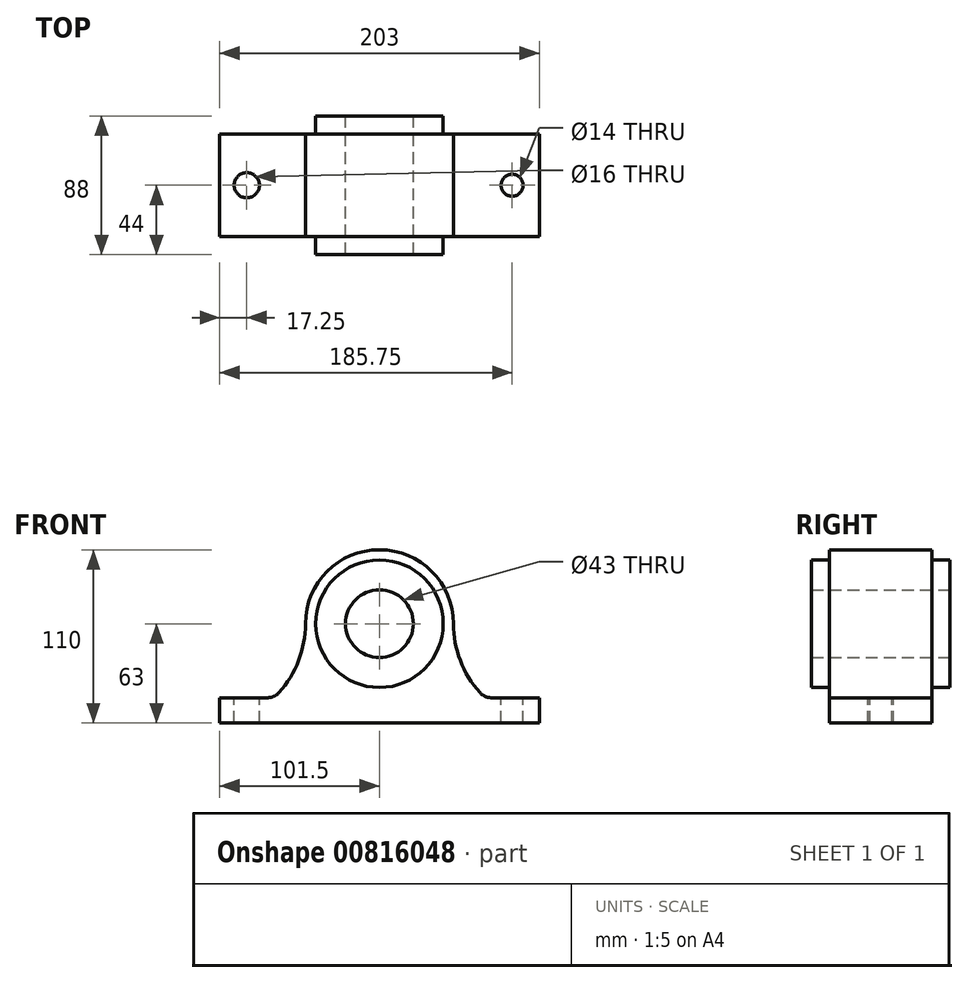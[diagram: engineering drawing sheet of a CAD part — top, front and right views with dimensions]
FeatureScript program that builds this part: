
annotation { "Feature Type Name" : "Feature", "Feature Type Description" : "" }
export const myFeature = defineFeature(function(context is Context, id is Id, definition is map)
    precondition{}
    {
        {
            var Q0;
            Q0=qCreatedBy(makeId("Front.planeOp"),FACE);
            var sketch = newSketch(context, id + "F0", { "sketchPlane" : qUnion([Q0])});
            skLineSegment(sketch, "E0", {"start": v(0, 0) * mm, "end": v(0, 110) * mm});
            skLineSegment(sketch, "E1", {"start": v(0, 0) * mm, "end": v(101.5, 0) * mm, "construction": true});
            skLineSegment(sketch, "E2", {"start": v(0, 0) * mm, "end": v(0, 16) * mm, "construction": true});
            skLineSegment(sketch, "E3.bottom", {"start": v(0, 0) * mm, "end": v(101.5, 0) * mm});
            skLineSegment(sketch, "E3.top", {"start": v(47, 16) * mm, "end": v(101.5, 16) * mm});
            skLineSegment(sketch, "E3.left", {"start": v(0, 0) * mm, "end": v(0, 16) * mm});
            skLineSegment(sketch, "E3.right", {"start": v(101.5, 0) * mm, "end": v(101.5, 16) * mm});
            skLineSegment(sketch, "E4.bottom", {"start": v(0, 0) * mm, "end": v(-101.5, 0) * mm});
            skLineSegment(sketch, "E4.top", {"start": v(-67, 16) * mm, "end": v(-101.5, 16) * mm});
            skLineSegment(sketch, "E4.right", {"start": v(-101.5, 0) * mm, "end": v(-101.5, 16) * mm});
            skLineSegment(sketch, "E5", {"start": v(0, 110) * mm, "end": v(0, 63) * mm});
            skCircle(sketch, "E6", {"center": v(0, 63) * mm, "radius": 21.5 * mm});
            skArc(sketch, "E7", {"start": v(47, 63) * mm, "mid": v(0, 110) * mm, "end": v(-47, 63) * mm});
            skLineSegment(sketch, "E8", {"start": v(0, 63) * mm, "end": v(-47, 63) * mm, "construction": true});
            skLineSegment(sketch, "E9", {"start": v(0, 63) * mm, "end": v(47, 63) * mm, "construction": true});
            skLineSegment(sketch, "E10", {"start": v(47, 63) * mm, "end": v(47, 16) * mm, "construction": true});
            skLineSegment(sketch, "E11", {"start": v(-47, 63) * mm, "end": v(-47, 16) * mm, "construction": true});
            skArc(sketch, "E12", {"start": v(-67, 16) * mm, "mid": v(-52.2, 37.46) * mm, "end": v(-47, 63) * mm});
            skArc(sketch, "E13", {"start": v(47, 63) * mm, "mid": v(52.2, 37.46) * mm, "end": v(67, 16) * mm});
            skSolve(sketch);
        }
        {
            var Q0;
            Q0=makeQuery(id+"F0.imprint","IMPRINT",FACE,{"disambiguationData":[TD([[makeQuery(id+"F0.imprint","IMPRINT",EDGE,{"derivedFrom":sQuery(id+"F0.wireOp",EDGE,"E3.bottom")}),1.0]])]});
            var Q1;
            Q1=makeQuery(id+"F0.imprint","IMPRINT",FACE,{"disambiguationData":[TD([[makeQuery(id+"F0.imprint","IMPRINT",EDGE,{"derivedFrom":sQuery(id+"F0.wireOp",EDGE,"E4.bottom")}),-1.0]])]});
            extrude(context, id + "F1", {"entities" : qUnion([Q0, Q1]), "depth" : 65 * mm, "offsetDistance" : 25 * mm});
        }
        {
            var Q0;
            Q0=makeQuery(id+"F1.opExtrude","CAP_FACE",FACE,{"disambiguationData":[OSD([sQuery(id+"F0.wireOp",EDGE,"E3.bottom"),sQuery(id+"F0.wireOp",EDGE,"E3.top"),sQuery(id+"F0.wireOp",EDGE,"E3.right"),sQuery(id+"F0.wireOp",EDGE,"E4.bottom"),sQuery(id+"F0.wireOp",EDGE,"E4.top"),sQuery(id+"F0.wireOp",EDGE,"E4.right"),sQuery(id+"F0.wireOp",EDGE,"E6"),sQuery(id+"F0.wireOp",EDGE,"E7"),sQuery(id+"F0.wireOp",EDGE,"E12"),sQuery(id+"F0.wireOp",EDGE,"E13")])],"isStart":false});
            var sketch = newSketch(context, id + "F2", { "sketchPlane" : qUnion([Q0])});
            skLineSegment(sketch, "E14", {"start": v(0, 0) * mm, "end": v(0, 63) * mm, "construction": true});
            skCircle(sketch, "E15", {"center": v(0, 63) * mm, "radius": 40.5 * mm});
            skCircle(sketch, "E16", {"center": v(0, 63) * mm, "radius": 21.5 * mm});
            skSolve(sketch);
        }
        {
            var Q0;
            Q0=makeQuery(id+"F2.imprint","IMPRINT",FACE,{"disambiguationData":[TD([[makeQuery(id+"F2.imprint","IMPRINT",EDGE,{"derivedFrom":sQuery(id+"F2.wireOp",EDGE,"E15")}),1.0]])]});
            extrude(context, id + "F3", {"entities" : qUnion([Q0]), "operationType" : NewBodyOperationType.ADD, "depth" : 11.5 * mm, "offsetDistance" : 25 * mm});
        }
        {
            var Q0;
            Q0=makeQuery(id+"F1.opExtrude","CAP_FACE",FACE,{"disambiguationData":[OSD([sQuery(id+"F0.wireOp",EDGE,"E3.bottom"),sQuery(id+"F0.wireOp",EDGE,"E3.top"),sQuery(id+"F0.wireOp",EDGE,"E3.right"),sQuery(id+"F0.wireOp",EDGE,"E4.bottom"),sQuery(id+"F0.wireOp",EDGE,"E4.top"),sQuery(id+"F0.wireOp",EDGE,"E4.right"),sQuery(id+"F0.wireOp",EDGE,"E6"),sQuery(id+"F0.wireOp",EDGE,"E7"),sQuery(id+"F0.wireOp",EDGE,"E12"),sQuery(id+"F0.wireOp",EDGE,"E13")])],"isStart":true});
            var sketch = newSketch(context, id + "F4", { "sketchPlane" : qUnion([Q0])});
            skLineSegment(sketch, "E17", {"start": v(0, 0) * mm, "end": v(0, 63) * mm, "construction": true});
            skCircle(sketch, "E18", {"center": v(0, 63) * mm, "radius": 40.5 * mm});
            skCircle(sketch, "E19", {"center": v(0, 63) * mm, "radius": 21.5 * mm});
            skSolve(sketch);
        }
        {
            var Q0;
            Q0=makeQuery(id+"F4.imprint","IMPRINT",FACE,{"disambiguationData":[TD([[makeQuery(id+"F4.imprint","IMPRINT",EDGE,{"derivedFrom":sQuery(id+"F4.wireOp",EDGE,"E18")}),1.0]])]});
            extrude(context, id + "F5", {"entities" : qUnion([Q0]), "operationType" : NewBodyOperationType.ADD, "depth" : 11.5 * mm, "offsetDistance" : 25 * mm});
        }
        {
            var Q0;
            Q0=makeQuery(id+"F1.opExtrude","SWEPT_FACE",FACE,{"disambiguationData":[OSD([sQuery(id+"F0.wireOp",EDGE,"E3.top")])]});
            var sketch = newSketch(context, id + "F6", { "sketchPlane" : qUnion([Q0])});
            skLineSegment(sketch, "E20", {"start": v(84.25, 0) * mm, "end": v(84.25, -65) * mm, "construction": true});
            skLineSegment(sketch, "E21", {"start": v(101.5, -32.5) * mm, "end": v(84.25, -32.5) * mm, "construction": true});
            skCircle(sketch, "E22", {"center": v(84.25, -32.5) * mm, "radius": 7 * mm});
            skSolve(sketch);
        }
        {
            var Q0;
            Q0=sQuery(id+"F6.wireOp",VERTEX,"E21.end");
            var Q1;
            Q1=makeQuery(id+"F1.opExtrude","SWEPT_BODY",BODY,{"disambiguationData":[OSD([sQuery(id+"F0.wireOp",EDGE,"E3.bottom"),sQuery(id+"F0.wireOp",EDGE,"E3.top"),sQuery(id+"F0.wireOp",EDGE,"E3.right"),sQuery(id+"F0.wireOp",EDGE,"E4.bottom"),sQuery(id+"F0.wireOp",EDGE,"E4.top"),sQuery(id+"F0.wireOp",EDGE,"E4.right"),sQuery(id+"F0.wireOp",EDGE,"E6"),sQuery(id+"F0.wireOp",EDGE,"E7"),sQuery(id+"F0.wireOp",EDGE,"E12"),sQuery(id+"F0.wireOp",EDGE,"E13")])]});
            hole(context, id + "F7", {"style" : HoleStyle.SIMPLE, "endStyle" : HoleEndStyle.THROUGH, "holeDiameter" : 14 * mm, "majorDiameter" : 5 * mm, "isTappedThrough" : true, "tappedDepth" : 12 * mm, "tapClearance" : 3, "locations" : qUnion([Q0]), "scope" : qUnion([Q1])});
        }
        {
            var Q0;
            Q0=makeQuery(id+"F1.opExtrude","SWEPT_FACE",FACE,{"disambiguationData":[OSD([sQuery(id+"F0.wireOp",EDGE,"E4.top")])]});
            var sketch = newSketch(context, id + "F8", { "sketchPlane" : qUnion([Q0])});
            skLineSegment(sketch, "E23", {"start": v(-101.5, -32.5) * mm, "end": v(-84.25, -32.5) * mm, "construction": true});
            skPoint(sketch, "E23.endSnap0", {"position": v(-84.25, 0) * mm});
            skLineSegment(sketch, "E24", {"start": v(-84.25, -32.5) * mm, "end": v(-84.25, 0) * mm, "construction": true});
            skCircle(sketch, "E25", {"center": v(-84.25, -32.5) * mm, "radius": 7 * mm});
            skSolve(sketch);
        }
        {
            var Q0;
            Q0=makeQuery(id+"F1.opExtrude","SWEPT_EDGE",EDGE,{"disambiguationData":[OSD([sQuery(id+"F0.wireOp",EDGE,"E4.top"),sQuery(id+"F0.wireOp",EDGE,"E12")])]});
            var Q1;
            Q1=makeQuery(id+"F1.opExtrude","SWEPT_EDGE",EDGE,{"disambiguationData":[OSD([sQuery(id+"F0.wireOp",EDGE,"E3.top"),sQuery(id+"F0.wireOp",EDGE,"E13")])]});
            fillet(context, id + "F9", {"entities" : qUnion([Q0, Q1]), "radius" : 10 * mm, "tangentPropagation" : true, "allowEdgeOverflow" : false});
        }
        {
            var Q0;
            Q0=sQuery(id+"F8.wireOp",VERTEX,"E23.end");
            var Q1;
            Q1=makeQuery(id+"F1.opExtrude","SWEPT_BODY",BODY,{"disambiguationData":[OSD([sQuery(id+"F0.wireOp",EDGE,"E3.bottom"),sQuery(id+"F0.wireOp",EDGE,"E3.top"),sQuery(id+"F0.wireOp",EDGE,"E3.right"),sQuery(id+"F0.wireOp",EDGE,"E4.bottom"),sQuery(id+"F0.wireOp",EDGE,"E4.top"),sQuery(id+"F0.wireOp",EDGE,"E4.right"),sQuery(id+"F0.wireOp",EDGE,"E6"),sQuery(id+"F0.wireOp",EDGE,"E7"),sQuery(id+"F0.wireOp",EDGE,"E12"),sQuery(id+"F0.wireOp",EDGE,"E13")])]});
            hole(context, id + "F10", {"style" : HoleStyle.SIMPLE, "endStyle" : HoleEndStyle.THROUGH, "holeDiameter" : 16 * mm, "majorDiameter" : 5 * mm, "isTappedThrough" : true, "tappedDepth" : 12 * mm, "tapClearance" : 3, "locations" : qUnion([Q0]), "scope" : qUnion([Q1])});
        }
    });
